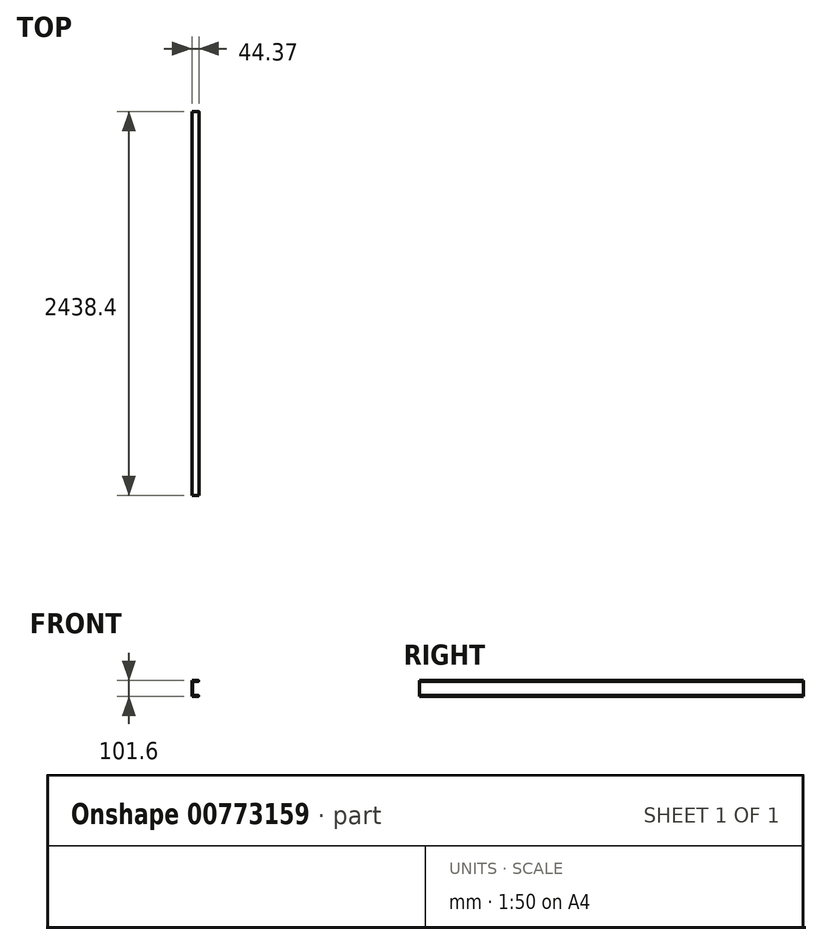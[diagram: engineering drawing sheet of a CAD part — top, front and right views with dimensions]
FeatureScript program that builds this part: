
annotation { "Feature Type Name" : "Feature", "Feature Type Description" : "" }
export const myFeature = defineFeature(function(context is Context, id is Id, definition is map)
    precondition{}
    {
        {
            var Q0;
            Q0=qCreatedBy(makeId("Front.planeOp"),FACE);
            var sketch = newSketch(context, id + "F0", { "sketchPlane" : qUnion([Q0])});
            skLineSegment(sketch, "E0", {"start": v(-24.06, 0) * mm, "end": v(-24.06, 50.8) * mm});
            skLineSegment(sketch, "E1", {"start": v(-24.06, 50.8) * mm, "end": v(17.77, 50.8) * mm});
            skArc(sketch, "E2", {"start": v(17.77, 50.8) * mm, "mid": v(20.31, 48.26) * mm, "end": v(17.77, 45.72) * mm});
            skLineSegment(sketch, "E3", {"start": v(17.77, 45.72) * mm, "end": v(-13.6, 41.34) * mm});
            skLineSegment(sketch, "E4", {"start": v(-17.79, 36.53) * mm, "end": v(-17.79, 0) * mm});
            skArc(sketch, "E5.MirrorCS", {"start": v(17.77, -50.8) * mm, "mid": v(20.31, -48.26) * mm, "end": v(17.77, -45.72) * mm});
            skLineSegment(sketch, "E6.MirrorCS", {"start": v(17.77, -45.72) * mm, "end": v(-13.6, -41.34) * mm});
            skLineSegment(sketch, "E7.MirrorCS", {"start": v(-17.79, -36.53) * mm, "end": v(-17.79, 0) * mm});
            skLineSegment(sketch, "E8.MirrorCS", {"start": v(-24.06, -50.8) * mm, "end": v(17.77, -50.8) * mm});
            skLineSegment(sketch, "E9.MirrorCS", {"start": v(-24.06, 0) * mm, "end": v(-24.06, -50.8) * mm});
            skPoint(sketch, "E10.visualSharp", {"position": v(-17.79, -40.75) * mm});
            skArc(sketch, "E10.filletArc", {"start": v(-17.79, -36.53) * mm, "mid": v(-16.6, -39.71) * mm, "end": v(-13.6, -41.34) * mm});
            skPoint(sketch, "E11.visualSharp", {"position": v(-17.79, 40.75) * mm});
            skArc(sketch, "E11.filletArc", {"start": v(-13.6, 41.34) * mm, "mid": v(-16.6, 39.71) * mm, "end": v(-17.79, 36.53) * mm});
            skSolve(sketch);
        }
        {
            var Q0;
            Q0=qSketchRegion(id+"F0",true);
            extrude(context, id + "F1", {"entities" : qUnion([Q0]), "depth" : 2438.4 * mm, "offsetDistance" : 25.4 * mm});
        }
    });
